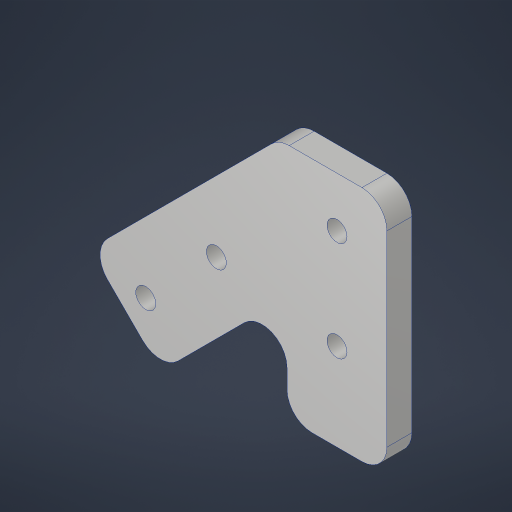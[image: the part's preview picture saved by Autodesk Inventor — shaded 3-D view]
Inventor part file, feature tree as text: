
AUTODESK INVENTOR PART (.ipt)
format: ipt  version: 2023.4 (Build 274418000, 418)  size: 214,528 bytes
history: native  units: in
note: dims shown in document units (in); Inventor stores cm internally (conversion verified against a paired STEP export)
features: sketch x2, projected_geometry x2, extrude x1, hole x1, fillet x1
ambient origin geometry x8: Origin, YZ Plane, XZ Plane, XY Plane, X Axis, Y Axis, Z Axis, Center Point
bodies: Solid1 (feature_tree)
feature tree (7):
  extrude  "Extrusion1"  Depth=2.25in
  hole  "Hole1"  [1 undecoded]
  fillet  "Fillet1"  Radius=1.0in
  sketch  "Sketch1"  dims[d0=45.0deg d1=2.25in]
  sketch  "Sketch2"  dims[d2=3.0in d3=0.125in d4=1.0in d5=1.0in d6=0.25in d7=0.0in d8=1.0in d9=1.0in d12=0.201in d13=0.75in d14=0.385in d15=0.25in d16=0.5635in d17=1.0in d18=0.8108in d19=0.5in d21=1.0in d22=0.25in]
  projected_geometry  "Project Cut Edges1"
  projected_geometry  "Project Cut Edges2"
note: 1 required parameter value undecoded (feature->parameter linkage not recoverable at this tier; creation-order binding heuristic only, values carry confidence <= 0.55)
